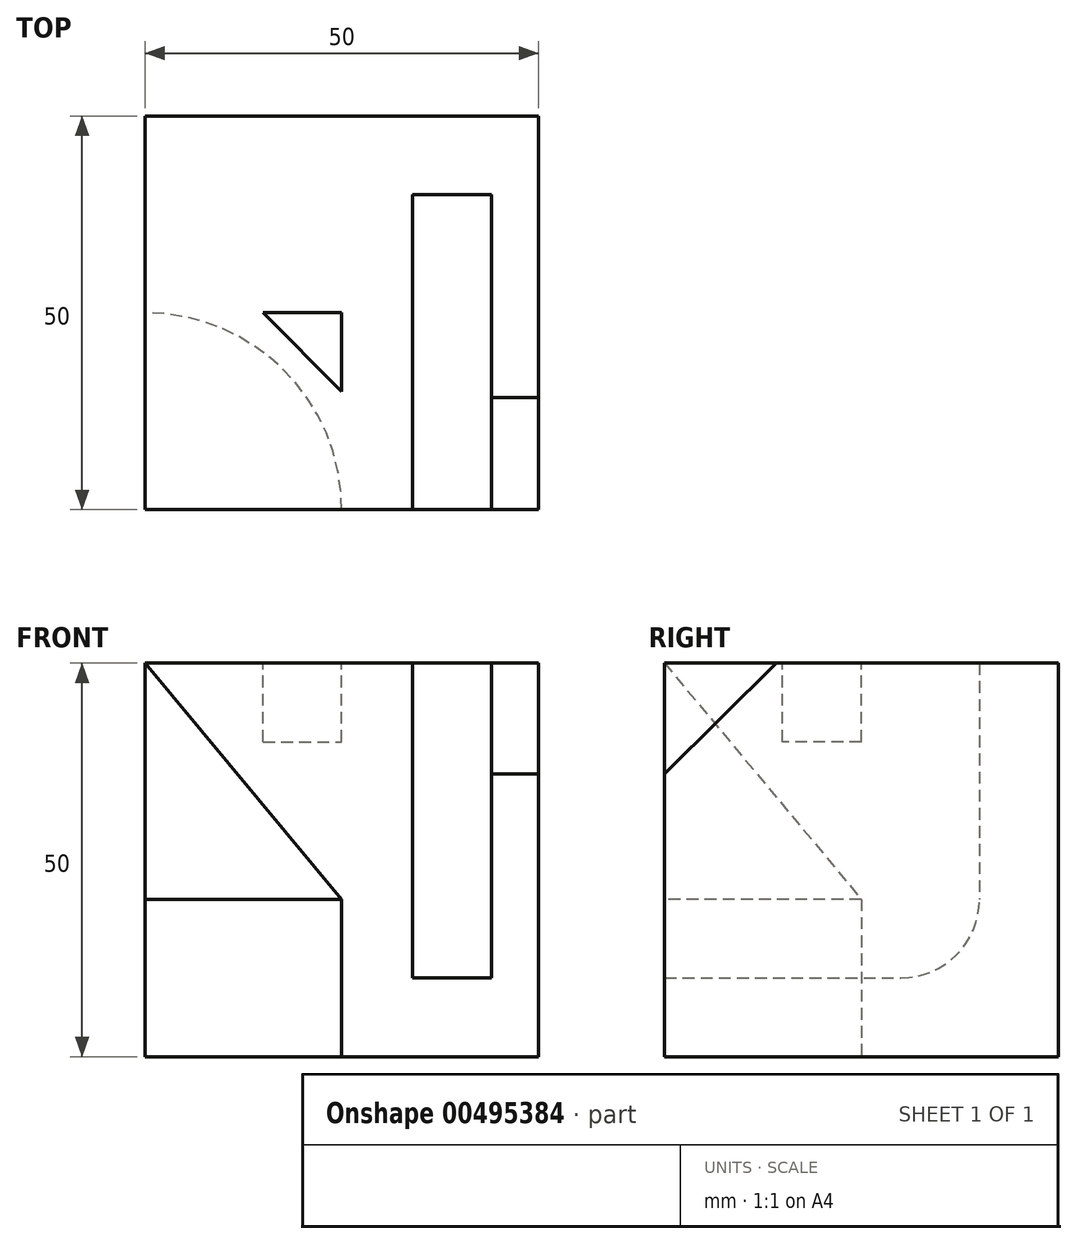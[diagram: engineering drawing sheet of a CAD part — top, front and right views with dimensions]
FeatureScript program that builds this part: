
annotation { "Feature Type Name" : "Feature", "Feature Type Description" : "" }
export const myFeature = defineFeature(function(context is Context, id is Id, definition is map)
    precondition{}
    {
        {
            var Q0;
            Q0=qCreatedBy(makeId("Right.planeOp"),FACE);
            var sketch = newSketch(context, id + "F0", { "sketchPlane" : qUnion([Q0])});
            skLineSegment(sketch, "E0.bottom", {"start": v(0, 0) * mm, "end": v(50, 0) * mm});
            skLineSegment(sketch, "E0.top", {"start": v(0, 50) * mm, "end": v(50, 50) * mm});
            skLineSegment(sketch, "E0.left", {"start": v(0, 0) * mm, "end": v(0, 50) * mm});
            skLineSegment(sketch, "E0.right", {"start": v(50, 0) * mm, "end": v(50, 50) * mm});
            skSolve(sketch);
        }
        {
            var Q0;
            Q0=makeQuery(id+"F0.imprint","IMPRINT",FACE,{"disambiguationData":[TD([[makeQuery(id+"F0.imprint","IMPRINT",EDGE,{"derivedFrom":sQuery(id+"F0.wireOp",EDGE,"E0.bottom")}),1.0]])]});
            extrude(context, id + "F1", {"entities" : qUnion([Q0]), "oppositeDirection" : true, "depth" : 16 * mm});
        }
        {
            var Q0;
            Q0=makeQuery(id+"F1.opExtrude","CAP_FACE",FACE,{"disambiguationData":[OSD([sQuery(id+"F0.wireOp",EDGE,"E0.bottom"),sQuery(id+"F0.wireOp",EDGE,"E0.top"),sQuery(id+"F0.wireOp",EDGE,"E0.left"),sQuery(id+"F0.wireOp",EDGE,"E0.right")])],"isStart":true});
            var sketch = newSketch(context, id + "F2", { "sketchPlane" : qUnion([Q0])});
            skLineSegment(sketch, "E1", {"start": v(0, 50) * mm, "end": v(14.2, 50) * mm});
            skLineSegment(sketch, "E2", {"start": v(14.2, 50) * mm, "end": v(0, 35.92) * mm});
            skLineSegment(sketch, "E3", {"start": v(0, 35.92) * mm, "end": v(0, 50) * mm});
            skSolve(sketch);
        }
        {
            var Q0;
            Q0=makeQuery(id+"F2.imprint","IMPRINT",FACE,{"disambiguationData":[TD([[makeQuery(id+"F2.imprint","IMPRINT",EDGE,{"derivedFrom":sQuery(id+"F2.wireOp",EDGE,"E1")}),-1.0]])]});
            extrude(context, id + "F3", {"entities" : qUnion([Q0]), "operationType" : NewBodyOperationType.REMOVE, "oppositeDirection" : true, "depth" : 6 * mm});
        }
        {
            var Q0;
            Q0=makeQuery(id+"F1.opExtrude","CAP_FACE",FACE,{"disambiguationData":[OSD([sQuery(id+"F0.wireOp",EDGE,"E0.bottom"),sQuery(id+"F0.wireOp",EDGE,"E0.top"),sQuery(id+"F0.wireOp",EDGE,"E0.left"),sQuery(id+"F0.wireOp",EDGE,"E0.right")])],"isStart":false});
            var sketch = newSketch(context, id + "F4", { "sketchPlane" : qUnion([Q0])});
            skLineSegment(sketch, "E4.bottom", {"start": v(0, 50) * mm, "end": v(-40, 50) * mm});
            skLineSegment(sketch, "E4.top", {"start": v(0, 10) * mm, "end": v(-30, 10) * mm});
            skLineSegment(sketch, "E4.left", {"start": v(0, 50) * mm, "end": v(0, 10) * mm});
            skLineSegment(sketch, "E4.right", {"start": v(-40, 50) * mm, "end": v(-40, 20) * mm});
            skPoint(sketch, "E5.visualSharp", {"position": v(-40, 10) * mm});
            skArc(sketch, "E5.filletArc", {"start": v(-40, 20) * mm, "mid": v(-37.07, 12.93) * mm, "end": v(-30, 10) * mm});
            skSolve(sketch);
        }
        {
            var Q0;
            Q0=makeQuery(id+"F4.imprint","IMPRINT",FACE,{"disambiguationData":[TD([[makeQuery(id+"F4.imprint","IMPRINT",EDGE,{"derivedFrom":sQuery(id+"F4.wireOp",EDGE,"E4.bottom")}),1.0]])]});
            extrude(context, id + "F5", {"entities" : qUnion([Q0]), "operationType" : NewBodyOperationType.REMOVE, "oppositeDirection" : true, "depth" : 10 * mm});
        }
        {
            var Q0;
            Q0=makeQuery(id+"F4.imprint","IMPRINT",FACE,{"disambiguationData":[TD([[makeQuery(id+"F4.imprint","IMPRINT",EDGE,{"derivedFrom":sQuery(id+"F4.wireOp",EDGE,"E4.bottom")}),1.0]])]});
            var Q1;
            {var subQ2=sQuery(id+"F4.wireOp",EDGE,"E4.top");Q1=makeQuery(id+"F4.imprint","IMPRINT",FACE,{"disambiguationData":[TD([[makeQuery(id+"F4.imprint","IMPRINT",EDGE,{"derivedFrom":subQ2}),1.0]])]});}
            extrude(context, id + "F6", {"entities" : qUnion([Q0, Q1]), "operationType" : NewBodyOperationType.ADD, "depth" : 34 * mm});
        }
        {
            var Q0;
            {var subQ0=sQuery(id+"F0.wireOp",EDGE,"E0.top");Q0=makeQuery(id+"F6.boolean.opBoolean","MERGE",FACE,{"derivedFrom":[makeQuery(id+"F1.opExtrude","SWEPT_FACE",FACE,{"disambiguationData":[OSD([subQ0])]}),makeQuery(id+"F6.opExtrude","SWEPT_FACE",FACE,{"disambiguationData":[OSD([subQ0,sQuery(id+"F4.wireOp",EDGE,"E4.bottom")])]})]});}
            var sketch = newSketch(context, id + "F7", { "sketchPlane" : qUnion([Q0])});
            skLineSegment(sketch, "E6.bottom", {"start": v(-50, 0) * mm, "end": v(-25, 0) * mm});
            skLineSegment(sketch, "E6.top", {"start": v(-50, 25) * mm, "end": v(-25, 25) * mm});
            skLineSegment(sketch, "E6.left", {"start": v(-50, 0) * mm, "end": v(-50, 25) * mm});
            skLineSegment(sketch, "E6.right", {"start": v(-25, 0) * mm, "end": v(-25, 25) * mm});
            skLineSegment(sketch, "E7", {"start": v(-25, 25) * mm, "end": v(-35, 25) * mm});
            skLineSegment(sketch, "E8", {"start": v(-35, 25) * mm, "end": v(-25, 15) * mm});
            skLineSegment(sketch, "E9", {"start": v(-25, 15) * mm, "end": v(-25, 25) * mm});
            skCircle(sketch, "E10", {"center": v(-50, 0) * mm, "radius": 15 * mm});
            skSolve(sketch);
        }
        {
            var Q0;
            {var subQ0=sQuery(id+"F0.wireOp",EDGE,"E0.bottom");Q0=makeQuery(id+"F6.boolean.opBoolean","MERGE",FACE,{"derivedFrom":[makeQuery(id+"F1.opExtrude","SWEPT_FACE",FACE,{"disambiguationData":[OSD([subQ0])]}),makeQuery(id+"F6.opExtrude","SWEPT_FACE",FACE,{"disambiguationData":[OSD([subQ0])]})]});}
            var sketch = newSketch(context, id + "F8", { "sketchPlane" : qUnion([Q0])});
            skCircle(sketch, "E11", {"center": v(-50, 0) * mm, "radius": 25 * mm});
            skSolve(sketch);
        }
        {
            var Q0;
            {var subQ0=sQuery(id+"F8.wireOp",EDGE,"E11");var subQ1=sQuery(id+"F0.wireOp",EDGE,"E0.bottom");var subQ2=makeQuery(id+"F6.opExtrude","CAP_EDGE",EDGE,{"disambiguationData":[OSD([subQ1])],"isStart":false});var subQ3=makeQuery(id+"F8.imprint","INTERSECT",VERTEX,{"derivedFrom":[subQ2,subQ0]});Q0=makeQuery(id+"F8.imprint","IMPRINT",FACE,{"disambiguationData":[TD([[makeQuery(id+"F8.imprint","IMPRINT",EDGE,{"disambiguationData":[TD([[subQ3,-1.0]])],"derivedFrom":subQ0}),1.0]])]});}
            extrude(context, id + "F9", {"entities" : qUnion([Q0]), "operationType" : NewBodyOperationType.REMOVE, "oppositeDirection" : true, "depth" : 20 * mm});
        }
        {
            var Q0;
            {var subQ2=sQuery(id+"F7.wireOp",EDGE,"E6.top");Q0=makeQuery(id+"F7.imprint","IMPRINT",FACE,{"disambiguationData":[TD([[makeQuery(id+"F7.imprint","IMPRINT",EDGE,{"derivedFrom":subQ2}),-1.0]])]});}
            extrude(context, id + "F10", {"entities" : qUnion([Q0]), "operationType" : NewBodyOperationType.REMOVE, "oppositeDirection" : true, "depth" : 10 * mm});
        }
        {
            var Q0;
            {var subQ0=sQuery(id+"F0.wireOp",EDGE,"E0.left");Q0=makeQuery(id+"F6.boolean.opBoolean","MERGE",FACE,{"derivedFrom":[makeQuery(id+"F1.opExtrude","SWEPT_FACE",FACE,{"disambiguationData":[OSD([subQ0])]}),makeQuery(id+"F6.opExtrude","SWEPT_FACE",FACE,{"disambiguationData":[OSD([subQ0,sQuery(id+"F4.wireOp",EDGE,"E4.left")])]})]});}
            var sketch = newSketch(context, id + "F11", { "sketchPlane" : qUnion([Q0])});
            skLineSegment(sketch, "E12", {"start": v(-50, 50) * mm, "end": v(-25, 20) * mm});
            skSolve(sketch);
        }
        {
            var Q0;
            Q0=makeQuery(id+"F6.opExtrude","CAP_FACE",FACE,{"disambiguationData":[OSD([sQuery(id+"F0.wireOp",EDGE,"E0.bottom"),sQuery(id+"F0.wireOp",EDGE,"E0.top"),sQuery(id+"F0.wireOp",EDGE,"E0.left"),sQuery(id+"F0.wireOp",EDGE,"E0.right"),sQuery(id+"F4.wireOp",EDGE,"E4.bottom"),sQuery(id+"F4.wireOp",EDGE,"E4.left")])],"isStart":false});
            var sketch = newSketch(context, id + "F12", { "sketchPlane" : qUnion([Q0])});
            skLineSegment(sketch, "E13", {"start": v(0, 50) * mm, "end": v(-25, 20) * mm});
            skSolve(sketch);
        }
        {
            var Q0;
            Q0=makeQuery(id+"F11.imprint","IMPRINT",FACE,{"disambiguationData":[TD([[makeQuery(id+"F11.imprint","IMPRINT",EDGE,{"derivedFrom":sQuery(id+"F11.wireOp",EDGE,"E12")}),-1.0]])]});
            var Q1;
            Q1=makeQuery(id+"F12.imprint","IMPRINT",FACE,{"disambiguationData":[TD([[makeQuery(id+"F12.imprint","IMPRINT",EDGE,{"derivedFrom":sQuery(id+"F12.wireOp",EDGE,"E13")}),1.0]])]});
            var Q2;
            Q2=makeQuery(id+"F9.boolean.opBoolean","COPY",EDGE,{"derivedFrom":makeQuery(id+"F9.opExtrude","CAP_EDGE",EDGE,{"disambiguationData":[OSD([sQuery(id+"F8.wireOp",EDGE,"E11")])],"isStart":false})});
            sweep(context, id + "F13", {"operationType" : NewBodyOperationType.REMOVE, "profiles" : qUnion([Q0, Q1]), "path" : qUnion([Q2])});
        }
    });
